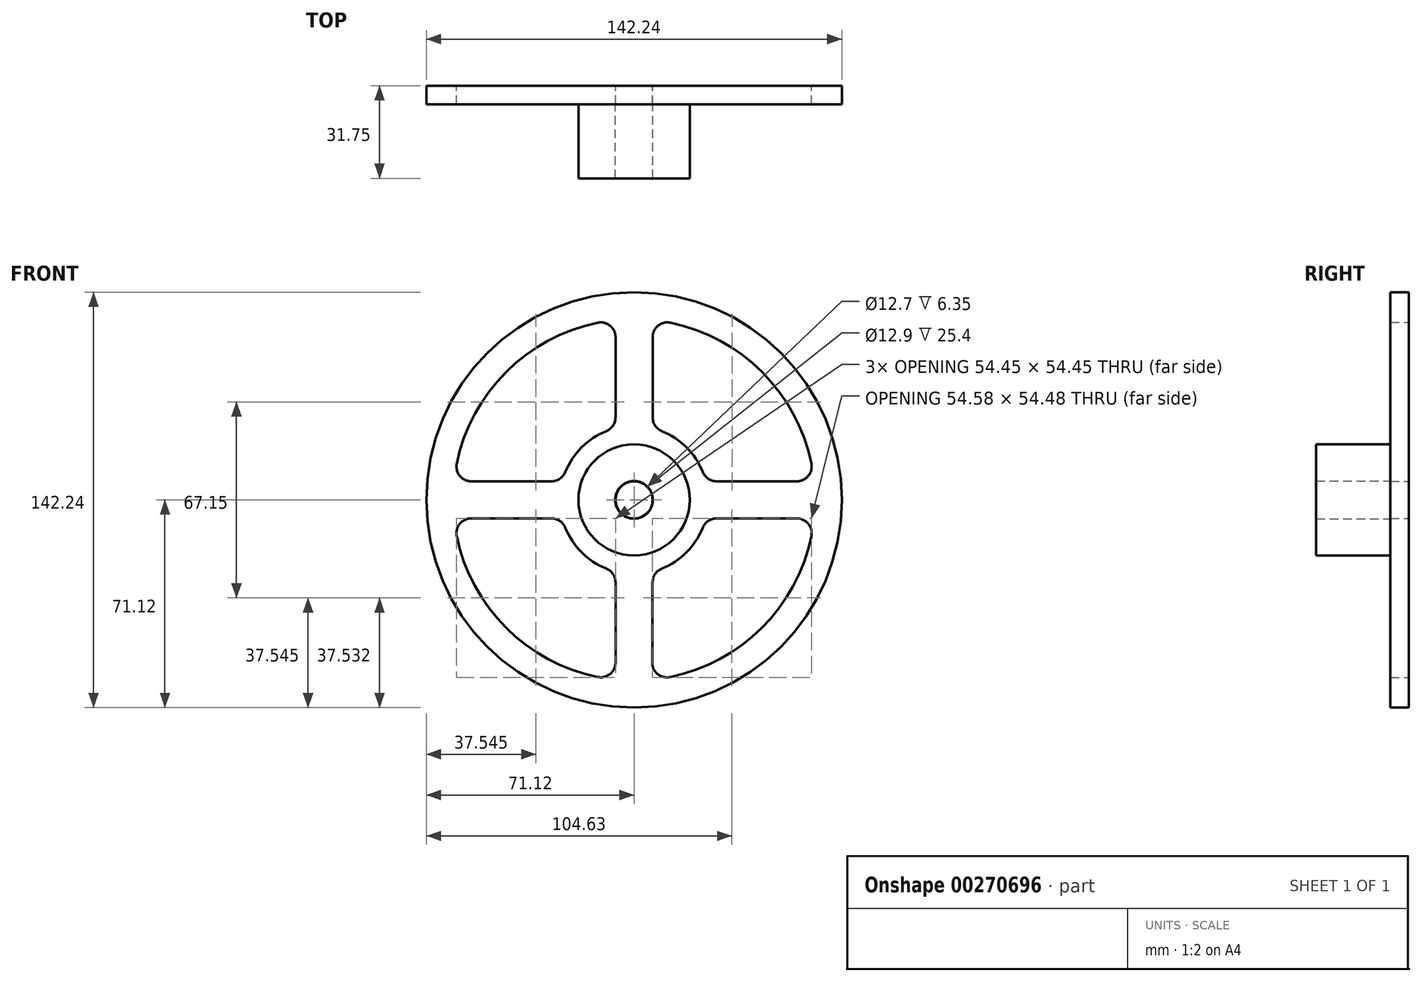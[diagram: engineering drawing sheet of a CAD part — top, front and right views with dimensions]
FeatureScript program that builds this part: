
annotation { "Feature Type Name" : "Feature", "Feature Type Description" : "" }
export const myFeature = defineFeature(function(context is Context, id is Id, definition is map)
    precondition{}
    {
        {
            var Q0;
            Q0=qCreatedBy(makeId("Front.planeOp"),FACE);
            var sketch = newSketch(context, id + "F0", { "sketchPlane" : qUnion([Q0])});
            skCircle(sketch, "E0", {"center": v(0, 0) * mm, "radius": 6.35 * mm});
            skCircle(sketch, "E1", {"center": v(0, 0) * mm, "radius": 71.12 * mm});
            skArc(sketch, "E2", {"start": v(-12.45, 60.7) * mm, "mid": v(-43.81, 43.81) * mm, "end": v(-60.7, 12.45) * mm});
            skArc(sketch, "E3", {"start": v(23.55, 9.53) * mm, "mid": v(17.96, 17.96) * mm, "end": v(9.53, 23.55) * mm});
            skLineSegment(sketch, "E4", {"start": v(-6.35, 28.26) * mm, "end": v(-6.35, 55.72) * mm});
            skLineSegment(sketch, "E5", {"start": v(6.35, 28.26) * mm, "end": v(6.35, 55.72) * mm});
            skLineSegment(sketch, "E6", {"start": v(-6.35, -28.26) * mm, "end": v(-6.35, -55.72) * mm});
            skLineSegment(sketch, "E7.trimOffspring", {"start": v(6.33, -28.24) * mm, "end": v(6.22, -55.73) * mm});
            skLineSegment(sketch, "E8", {"start": v(-28.26, 6.35) * mm, "end": v(-55.72, 6.35) * mm});
            skLineSegment(sketch, "E9", {"start": v(28.26, 6.35) * mm, "end": v(55.72, 6.35) * mm});
            skLineSegment(sketch, "E10", {"start": v(-28.26, -6.35) * mm, "end": v(-55.72, -6.35) * mm});
            skLineSegment(sketch, "E11", {"start": v(28.26, -6.35) * mm, "end": v(55.72, -6.35) * mm});
            skPoint(sketch, "E12.orphan", {"position": v(0, -6.35) * mm});
            skPoint(sketch, "E13.orphan", {"position": v(0, 6.35) * mm});
            skArc(sketch, "E14.trimOffspring", {"start": v(-9.53, 23.55) * mm, "mid": v(-17.96, 17.96) * mm, "end": v(-23.55, 9.52) * mm});
            skArc(sketch, "E15.trimOffspring", {"start": v(-23.55, -9.53) * mm, "mid": v(-17.96, -17.96) * mm, "end": v(-9.52, -23.55) * mm});
            skArc(sketch, "E16.trimOffspring", {"start": v(9.51, -23.55) * mm, "mid": v(17.96, -17.97) * mm, "end": v(23.55, -9.53) * mm});
            skArc(sketch, "E17.trimOffspring", {"start": v(60.7, 12.45) * mm, "mid": v(43.81, 43.81) * mm, "end": v(12.45, 60.7) * mm});
            skArc(sketch, "E18.trimOffspring", {"start": v(12.3, -60.73) * mm, "mid": v(43.76, -43.86) * mm, "end": v(60.7, -12.45) * mm});
            skArc(sketch, "E19.trimOffspring", {"start": v(-60.7, -12.45) * mm, "mid": v(-43.81, -43.81) * mm, "end": v(-12.45, -60.7) * mm});
            skPoint(sketch, "E20.visualSharp", {"position": v(61.64, 6.35) * mm});
            skArc(sketch, "E20.filletArc", {"start": v(55.72, 6.35) * mm, "mid": v(59.66, 8.22) * mm, "end": v(60.7, 12.45) * mm});
            skPoint(sketch, "E21.visualSharp", {"position": v(24.6, 6.35) * mm});
            skArc(sketch, "E21.filletArc", {"start": v(23.55, 9.53) * mm, "mid": v(25.42, 7.22) * mm, "end": v(28.26, 6.35) * mm});
            skPoint(sketch, "E22.visualSharp", {"position": v(6.35, 61.64) * mm});
            skArc(sketch, "E22.filletArc", {"start": v(12.45, 60.7) * mm, "mid": v(8.22, 59.66) * mm, "end": v(6.35, 55.72) * mm});
            skPoint(sketch, "E23.visualSharp", {"position": v(6.35, 24.6) * mm});
            skArc(sketch, "E23.filletArc", {"start": v(6.35, 28.26) * mm, "mid": v(7.22, 25.42) * mm, "end": v(9.53, 23.55) * mm});
            skPoint(sketch, "E24.visualSharp", {"position": v(-6.35, 61.64) * mm});
            skArc(sketch, "E24.filletArc", {"start": v(-6.35, 55.72) * mm, "mid": v(-8.22, 59.66) * mm, "end": v(-12.45, 60.7) * mm});
            skPoint(sketch, "E25.visualSharp", {"position": v(-24.6, 6.35) * mm});
            skArc(sketch, "E25.filletArc", {"start": v(-28.26, 6.35) * mm, "mid": v(-25.42, 7.22) * mm, "end": v(-23.55, 9.53) * mm});
            skPoint(sketch, "E26.visualSharp", {"position": v(-6.35, 24.6) * mm});
            skArc(sketch, "E26.filletArc", {"start": v(-9.53, 23.55) * mm, "mid": v(-7.22, 25.42) * mm, "end": v(-6.35, 28.26) * mm});
            skPoint(sketch, "E27.visualSharp", {"position": v(-61.64, 6.35) * mm});
            skArc(sketch, "E27.filletArc", {"start": v(-60.7, 12.45) * mm, "mid": v(-59.66, 8.22) * mm, "end": v(-55.72, 6.35) * mm});
            skPoint(sketch, "E28.visualSharp", {"position": v(-24.6, -6.35) * mm});
            skArc(sketch, "E28.filletArc", {"start": v(-23.55, -9.52) * mm, "mid": v(-25.42, -7.22) * mm, "end": v(-28.26, -6.35) * mm});
            skPoint(sketch, "E29.visualSharp", {"position": v(-6.35, -24.6) * mm});
            skArc(sketch, "E29.filletArc", {"start": v(-6.35, -28.26) * mm, "mid": v(-7.22, -25.42) * mm, "end": v(-9.53, -23.55) * mm});
            skPoint(sketch, "E30.visualSharp", {"position": v(61.64, -6.35) * mm});
            skArc(sketch, "E30.filletArc", {"start": v(60.7, -12.45) * mm, "mid": v(59.66, -8.22) * mm, "end": v(55.72, -6.35) * mm});
            skPoint(sketch, "E31.visualSharp", {"position": v(6.35, -24.6) * mm});
            skArc(sketch, "E31.filletArc", {"start": v(9.51, -23.55) * mm, "mid": v(7.2, -25.41) * mm, "end": v(6.33, -28.24) * mm});
            skPoint(sketch, "E32.visualSharp", {"position": v(-61.64, -6.35) * mm});
            skArc(sketch, "E32.filletArc", {"start": v(-55.72, -6.35) * mm, "mid": v(-59.66, -8.22) * mm, "end": v(-60.7, -12.45) * mm});
            skPoint(sketch, "E33.visualSharp", {"position": v(24.6, -6.35) * mm});
            skArc(sketch, "E33.filletArc", {"start": v(28.26, -6.35) * mm, "mid": v(25.42, -7.22) * mm, "end": v(23.55, -9.53) * mm});
            skPoint(sketch, "E34.visualSharp", {"position": v(6.2, -61.65) * mm});
            skArc(sketch, "E34.filletArc", {"start": v(6.22, -55.73) * mm, "mid": v(8.08, -59.67) * mm, "end": v(12.3, -60.73) * mm});
            skPoint(sketch, "E35.visualSharp", {"position": v(-6.35, -61.64) * mm});
            skArc(sketch, "E35.filletArc", {"start": v(-12.45, -60.7) * mm, "mid": v(-8.22, -59.66) * mm, "end": v(-6.35, -55.72) * mm});
            skSolve(sketch);
        }
        {
            var Q0;
            Q0 = qSketchRegion(id + "F0", true);
            extrude(context, id + "F1", {"entities" : qUnion([Q0]), "depth" : 6.35 * mm});
        }
        {
            var Q0;
            Q0=makeQuery(id+"F1.opExtrude","CAP_FACE",FACE,{"disambiguationData":[OSD([sQuery(id+"F0.wireOp",EDGE,"E0"),sQuery(id+"F0.wireOp",EDGE,"E1"),sQuery(id+"F0.wireOp",EDGE,"E2"),sQuery(id+"F0.wireOp",EDGE,"E3"),sQuery(id+"F0.wireOp",EDGE,"E4"),sQuery(id+"F0.wireOp",EDGE,"E5"),sQuery(id+"F0.wireOp",EDGE,"E6"),sQuery(id+"F0.wireOp",EDGE,"E7.trimOffspring"),sQuery(id+"F0.wireOp",EDGE,"E8"),sQuery(id+"F0.wireOp",EDGE,"E9"),sQuery(id+"F0.wireOp",EDGE,"E10"),sQuery(id+"F0.wireOp",EDGE,"E11"),sQuery(id+"F0.wireOp",EDGE,"E14.trimOffspring"),sQuery(id+"F0.wireOp",EDGE,"E15.trimOffspring"),sQuery(id+"F0.wireOp",EDGE,"E16.trimOffspring"),sQuery(id+"F0.wireOp",EDGE,"E17.trimOffspring"),sQuery(id+"F0.wireOp",EDGE,"E18.trimOffspring"),sQuery(id+"F0.wireOp",EDGE,"E19.trimOffspring"),sQuery(id+"F0.wireOp",EDGE,"E20.filletArc"),sQuery(id+"F0.wireOp",EDGE,"E21.filletArc"),sQuery(id+"F0.wireOp",EDGE,"E22.filletArc"),sQuery(id+"F0.wireOp",EDGE,"E23.filletArc"),sQuery(id+"F0.wireOp",EDGE,"E24.filletArc"),sQuery(id+"F0.wireOp",EDGE,"E25.filletArc"),sQuery(id+"F0.wireOp",EDGE,"E26.filletArc"),sQuery(id+"F0.wireOp",EDGE,"E27.filletArc"),sQuery(id+"F0.wireOp",EDGE,"E28.filletArc"),sQuery(id+"F0.wireOp",EDGE,"E29.filletArc"),sQuery(id+"F0.wireOp",EDGE,"E30.filletArc"),sQuery(id+"F0.wireOp",EDGE,"E31.filletArc"),sQuery(id+"F0.wireOp",EDGE,"E32.filletArc"),sQuery(id+"F0.wireOp",EDGE,"E33.filletArc"),sQuery(id+"F0.wireOp",EDGE,"E34.filletArc"),sQuery(id+"F0.wireOp",EDGE,"E35.filletArc")])],"isStart":false});
            var sketch = newSketch(context, id + "F2", { "sketchPlane" : qUnion([Q0])});
            skCircle(sketch, "E36", {"center": v(0, 0) * mm, "radius": 19.05 * mm});
            skCircle(sketch, "E37", {"center": v(0, 0) * mm, "radius": 6.45 * mm});
            skSolve(sketch);
        }
        {
            var Q0;
            Q0 = qSketchRegion(id + "F2", true);
            extrude(context, id + "F3", {"entities" : qUnion([Q0]), "operationType" : NewBodyOperationType.ADD, "depth" : 25.4 * mm});
        }
    });
